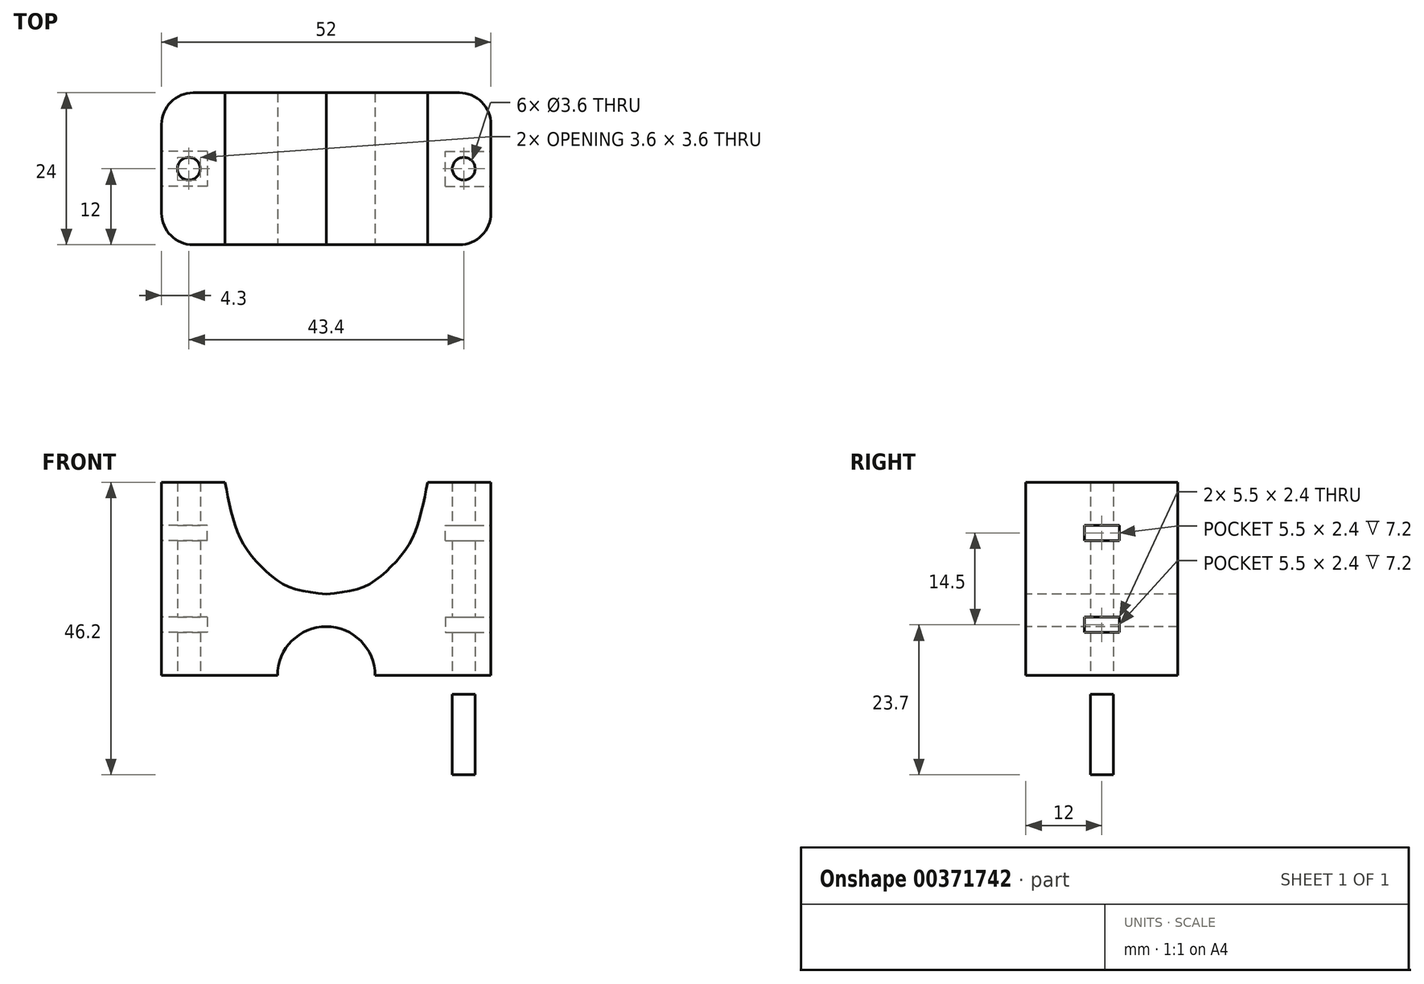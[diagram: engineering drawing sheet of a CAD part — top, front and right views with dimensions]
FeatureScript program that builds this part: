
annotation { "Feature Type Name" : "Feature", "Feature Type Description" : "" }
export const myFeature = defineFeature(function(context is Context, id is Id, definition is map)
    precondition{}
    {
        {
            var Q0;
            Q0=qCreatedBy(makeId("Top.planeOp"),FACE);
            var sketch = newSketch(context, id + "F0", { "sketchPlane" : qUnion([Q0])});
            skLineSegment(sketch, "E0.bottom", {"start": v(-21, 12) * mm, "end": v(21, 12) * mm});
            skLineSegment(sketch, "E0.top", {"start": v(-21, -12) * mm, "end": v(21, -12) * mm});
            skLineSegment(sketch, "E0.left", {"start": v(-26, 7) * mm, "end": v(-26, -7) * mm});
            skLineSegment(sketch, "E0.right", {"start": v(26, 7) * mm, "end": v(26, -7) * mm});
            skPoint(sketch, "E0.middle", {"position": v(0, 0) * mm});
            skLineSegment(sketch, "E1", {"start": v(0, 0) * mm, "end": v(-21.7, 0) * mm, "construction": true});
            skCircle(sketch, "E2", {"center": v(-21.7, 0) * mm, "radius": 1.8 * mm});
            skCircle(sketch, "E3.MirrorC", {"center": v(21.7, 0) * mm, "radius": 1.8 * mm});
            skPoint(sketch, "E4.visualSharp", {"position": v(-26, 12) * mm});
            skArc(sketch, "E4.filletArc", {"start": v(-21, 12) * mm, "mid": v(-24.54, 10.54) * mm, "end": v(-26, 7) * mm});
            skPoint(sketch, "E5.visualSharp", {"position": v(-26, -12) * mm});
            skArc(sketch, "E5.filletArc", {"start": v(-26, -7) * mm, "mid": v(-24.54, -10.54) * mm, "end": v(-21, -12) * mm});
            skPoint(sketch, "E6.visualSharp", {"position": v(26, -12) * mm});
            skArc(sketch, "E6.filletArc", {"start": v(21, -12) * mm, "mid": v(24.54, -10.54) * mm, "end": v(26, -7) * mm});
            skPoint(sketch, "E7.visualSharp", {"position": v(26, 12) * mm});
            skArc(sketch, "E7.filletArc", {"start": v(26, 7) * mm, "mid": v(24.54, 10.54) * mm, "end": v(21, 12) * mm});
            skSolve(sketch);
        }
        {
            var Q0;
            Q0 = qSketchRegion(id + "F0", true);
            extrude(context, id + "F1", {"entities" : qUnion([Q0]), "depth" : (15.7 / 2 + 22.65) * mm, "offsetDistance" : 25 * mm});
        }
        {
            var Q0;
            Q0=makeQuery(id+"F1.opExtrude","SWEPT_FACE",FACE,{"disambiguationData":[OSD([sQuery(id+"F0.wireOp",EDGE,"E0.top")])]});
            var sketch = newSketch(context, id + "F2", { "sketchPlane" : qUnion([Q0])});
            skArc(sketch, "E8", {"start": v(7.7, 0) * mm, "mid": v(0, 7.7) * mm, "end": v(-7.7, 0) * mm});
            skLineSegment(sketch, "E9", {"start": v(-7.7, 0) * mm, "end": v(-21, 0) * mm});
            skLineSegment(sketch, "E10", {"start": v(-21, 0) * mm, "end": v(-21, 30.5) * mm});
            skLineSegment(sketch, "E11", {"start": v(-21, 30.5) * mm, "end": v(-21, 30.5) * mm});
            skLineSegment(sketch, "E12", {"start": v(-21, 30.5) * mm, "end": v(-21, 0) * mm});
            skLineSegment(sketch, "E13", {"start": v(7.7, 0) * mm, "end": v(-21, 0) * mm});
            skLineSegment(sketch, "E14", {"start": v(0, 30.5) * mm, "end": v(0, 12.85) * mm, "construction": true});
            skLineSegment(sketch, "E15", {"start": v(16, 30.5) * mm, "end": v(0, 30.5) * mm});
            skLineSegment(sketch, "E16.MirrorCS", {"start": v(-16, 30.5) * mm, "end": v(0, 30.5) * mm});
            skFitSpline(sketch, "E17", {"points": [v(-16, 30.5) * mm, v(-14.81, 25.12) * mm, v(-12.95, 20.5) * mm, v(-9.64, 16.6) * mm, v(-5.78, 13.92) * mm, v(0, 12.85) * mm], "startDerivative": vector(5.26, -26.66) * mm, "endDerivative": vector(29.07, -2.83) * mm});
            skPoint(sketch, "E18.MirrorCS.start.orphan", {"position": v(-16, 12.85) * mm});
            skFitSpline(sketch, "E19.MirrorCS", {"points": [v(16, 30.5) * mm, v(14.81, 25.12) * mm, v(12.95, 20.5) * mm, v(9.64, 16.6) * mm, v(5.78, 13.92) * mm, v(0, 12.85) * mm], "startDerivative": vector(-5.26, -26.66) * mm, "endDerivative": vector(-29.07, -2.83) * mm});
            skPoint(sketch, "E20.start.orphan", {"position": v(16, 12.85) * mm});
            skSolve(sketch);
        }
        {
            var Q0;
            {var subQ0=sQuery(id+"F2.wireOp",EDGE,"E8");Q0=makeQuery(id+"F2.imprint","IMPRINT",FACE,{"disambiguationData":[TD([[makeQuery(id+"F2.imprint","IMPRINT",EDGE,{"derivedFrom":subQ0}),1.0]])]});}
            extrude(context, id + "F3", {"entities" : qUnion([Q0]), "operationType" : NewBodyOperationType.REMOVE, "oppositeDirection" : true, "depth" : 24 * mm, "offsetDistance" : 25 * mm});
        }
        {
            var Q0;
            Q0=makeQuery(id+"F2.imprint","IMPRINT",FACE,{"disambiguationData":[TD([[makeQuery(id+"F2.imprint","IMPRINT",EDGE,{"derivedFrom":sQuery(id+"F2.wireOp",EDGE,"E15")}),-1.0]])]});
            extrude(context, id + "F4", {"entities" : qUnion([Q0]), "operationType" : NewBodyOperationType.REMOVE, "oppositeDirection" : true, "depth" : 24 * mm, "offsetDistance" : 25 * mm});
        }
        {
            var Q0;
            Q0=makeQuery(id+"F1.opExtrude","SWEPT_FACE",FACE,{"disambiguationData":[OSD([sQuery(id+"F0.wireOp",EDGE,"E0.left")])]});
            var sketch = newSketch(context, id + "F5", { "sketchPlane" : qUnion([Q0])});
            skLineSegment(sketch, "E21", {"start": v(0, 0) * mm, "end": v(0, 8) * mm, "construction": true});
            skLineSegment(sketch, "E22.bottom", {"start": v(-2.75, 9.2) * mm, "end": v(2.75, 9.2) * mm});
            skLineSegment(sketch, "E22.top", {"start": v(-2.75, 6.8) * mm, "end": v(2.75, 6.8) * mm});
            skLineSegment(sketch, "E22.left", {"start": v(-2.75, 9.2) * mm, "end": v(-2.75, 6.8) * mm});
            skLineSegment(sketch, "E22.right", {"start": v(2.75, 9.2) * mm, "end": v(2.75, 6.8) * mm});
            skPoint(sketch, "E22.middle", {"position": v(0, 8) * mm});
            skLineSegment(sketch, "E23", {"start": v(-7, 15.25) * mm, "end": v(7, 15.25) * mm, "construction": true});
            skLineSegment(sketch, "E24.MirrorCS", {"start": v(-2.75, 21.3) * mm, "end": v(2.75, 21.3) * mm});
            skLineSegment(sketch, "E25.MirrorCS", {"start": v(2.75, 21.3) * mm, "end": v(2.75, 23.7) * mm});
            skLineSegment(sketch, "E26.MirrorCS", {"start": v(-2.75, 23.7) * mm, "end": v(2.75, 23.7) * mm});
            skLineSegment(sketch, "E27.MirrorCS", {"start": v(-2.75, 21.3) * mm, "end": v(-2.75, 23.7) * mm});
            skSolve(sketch);
        }
        {
            var Q0;
            Q0=makeQuery(id+"F5.imprint","IMPRINT",FACE,{"disambiguationData":[TD([[makeQuery(id+"F5.imprint","IMPRINT",EDGE,{"derivedFrom":sQuery(id+"F5.wireOp",EDGE,"E22.bottom")}),-1.0]])]});
            var Q1;
            Q1=makeQuery(id+"F5.imprint","IMPRINT",FACE,{"disambiguationData":[TD([[makeQuery(id+"F5.imprint","IMPRINT",EDGE,{"derivedFrom":sQuery(id+"F5.wireOp",EDGE,"E24.MirrorCS")}),1.0]])]});
            extrude(context, id + "F6", {"entities" : qUnion([Q0, Q1]), "operationType" : NewBodyOperationType.REMOVE, "oppositeDirection" : true, "depth" : (2.5 + 1.7 + 3) * mm, "offsetDistance" : 25 * mm});
        }
        {
            var Q0;
            Q0=makeQuery(id+"F1.opExtrude","SWEPT_FACE",FACE,{"disambiguationData":[OSD([sQuery(id+"F0.wireOp",EDGE,"E0.right")])]});
            var sketch = newSketch(context, id + "F7", { "sketchPlane" : qUnion([Q0])});
            skLineSegment(sketch, "E28", {"start": v(-7, 15.25) * mm, "end": v(7, 15.25) * mm, "construction": true});
            skLineSegment(sketch, "E29", {"start": v(0, 0) * mm, "end": v(0, 8) * mm, "construction": true});
            skLineSegment(sketch, "E30.bottom", {"start": v(-2.75, 9.2) * mm, "end": v(2.75, 9.2) * mm});
            skLineSegment(sketch, "E30.top", {"start": v(-2.75, 6.8) * mm, "end": v(2.75, 6.8) * mm});
            skLineSegment(sketch, "E30.left", {"start": v(-2.75, 9.2) * mm, "end": v(-2.75, 6.8) * mm});
            skLineSegment(sketch, "E30.right", {"start": v(2.75, 9.2) * mm, "end": v(2.75, 6.8) * mm});
            skPoint(sketch, "E30.middle", {"position": v(0, 8) * mm});
            skLineSegment(sketch, "E31.MirrorCS", {"start": v(-2.75, 21.3) * mm, "end": v(2.75, 21.3) * mm});
            skLineSegment(sketch, "E32.MirrorCS", {"start": v(2.75, 21.3) * mm, "end": v(2.75, 23.7) * mm});
            skLineSegment(sketch, "E33.MirrorCS", {"start": v(-2.75, 23.7) * mm, "end": v(2.75, 23.7) * mm});
            skLineSegment(sketch, "E34.MirrorCS", {"start": v(-2.75, 21.3) * mm, "end": v(-2.75, 23.7) * mm});
            skSolve(sketch);
        }
        {
            var Q0;
            Q0=makeQuery(id+"F7.imprint","IMPRINT",FACE,{"disambiguationData":[TD([[makeQuery(id+"F7.imprint","IMPRINT",EDGE,{"derivedFrom":sQuery(id+"F7.wireOp",EDGE,"E30.bottom")}),-1.0]])]});
            var Q1;
            Q1=makeQuery(id+"F7.imprint","IMPRINT",FACE,{"disambiguationData":[TD([[makeQuery(id+"F7.imprint","IMPRINT",EDGE,{"derivedFrom":sQuery(id+"F7.wireOp",EDGE,"E31.MirrorCS")}),1.0]])]});
            extrude(context, id + "F8", {"entities" : qUnion([Q0, Q1]), "operationType" : NewBodyOperationType.REMOVE, "oppositeDirection" : true, "depth" : (2.5 + 1.7 + 3) * mm, "offsetDistance" : 25 * mm});
        }
        {
            var Q0;
            Q0=qCreatedBy(makeId("Front.planeOp"),FACE);
            var sketch = newSketch(context, id + "F9", { "sketchPlane" : qUnion([Q0])});
            skLineSegment(sketch, "E35", {"start": v(0, 0) * mm, "end": v(0, -7.85) * mm, "construction": true});
            skLineSegment(sketch, "E36.bottom", {"start": v(-7.7, 0) * mm, "end": v(7.7, 0) * mm});
            skLineSegment(sketch, "E36.top", {"start": v(-26, -15.7) * mm, "end": v(26, -15.7) * mm});
            skLineSegment(sketch, "E36.left", {"start": v(-26, 0) * mm, "end": v(-26, -15.7) * mm});
            skLineSegment(sketch, "E36.right", {"start": v(26, -3) * mm, "end": v(26, -15.7) * mm});
            skPoint(sketch, "E36.middle", {"position": v(0, -7.85) * mm});
            skArc(sketch, "E37", {"start": v(-7.1, -3) * mm, "mid": v(0, -7.7) * mm, "end": v(7.1, -3) * mm});
            skLineSegment(sketch, "E38", {"start": v(-26, -3) * mm, "end": v(-7.1, -3) * mm});
            skLineSegment(sketch, "E39.MirrorCS", {"start": v(26, -3) * mm, "end": v(7.1, -3) * mm});
            skArc(sketch, "E40.trimOffspring", {"start": v(7.7, 0) * mm, "mid": v(0, 7.7) * mm, "end": v(-7.7, 0) * mm});
            skPoint(sketch, "E41.orphan", {"position": v(26, 0) * mm});
            skSolve(sketch);
        }
        {
            var Q0;
            Q0=makeQuery(id+"F9.imprint","IMPRINT",FACE,{"disambiguationData":[TD([[makeQuery(id+"F9.imprint","IMPRINT",EDGE,{"derivedFrom":sQuery(id+"F9.wireOp",EDGE,"E36.top")}),1.0]])]});
            extrude(context, id + "F10", {"entities" : qUnion([Q0]), "endBound" : BoundingType.SYMMETRIC, "depth" : 24 * mm, "offsetDistance" : 25 * mm});
        }
        {
            var Q0;
            Q0=makeQuery(id+"F10.opExtrude","SWEPT_FACE",FACE,{"disambiguationData":[OSD([sQuery(id+"F9.wireOp",EDGE,"E36.top")])]});
            var sketch = newSketch(context, id + "F11", { "sketchPlane" : qUnion([Q0])});
            skLineSegment(sketch, "E42.bottom", {"start": v(-21, 12) * mm, "end": v(21, 12) * mm});
            skLineSegment(sketch, "E42.top", {"start": v(-21, -12) * mm, "end": v(21, -12) * mm});
            skLineSegment(sketch, "E42.left", {"start": v(-26, 7) * mm, "end": v(-26, -7) * mm});
            skLineSegment(sketch, "E42.right", {"start": v(26, 7) * mm, "end": v(26, -7) * mm});
            skPoint(sketch, "E43.visualSharp", {"position": v(-26, 12) * mm});
            skArc(sketch, "E43.filletArc", {"start": v(-21, 12) * mm, "mid": v(-24.54, 10.54) * mm, "end": v(-26, 7) * mm});
            skPoint(sketch, "E44.visualSharp", {"position": v(-26, -12) * mm});
            skArc(sketch, "E44.filletArc", {"start": v(-26, -7) * mm, "mid": v(-24.54, -10.54) * mm, "end": v(-21, -12) * mm});
            skPoint(sketch, "E45.visualSharp", {"position": v(26, -12) * mm});
            skArc(sketch, "E45.filletArc", {"start": v(21, -12) * mm, "mid": v(24.54, -10.54) * mm, "end": v(26, -7) * mm});
            skPoint(sketch, "E46.visualSharp", {"position": v(26, 12) * mm});
            skArc(sketch, "E46.filletArc", {"start": v(26, 7) * mm, "mid": v(24.54, 10.54) * mm, "end": v(21, 12) * mm});
            skSolve(sketch);
        }
        {
            var Q0;
            {var subQ0=sQuery(id+"F11.wireOp",EDGE,"E46.filletArc");Q0=makeQuery(id+"F11.imprint","IMPRINT",FACE,{"disambiguationData":[TD([[makeQuery(id+"F11.imprint","IMPRINT",EDGE,{"derivedFrom":subQ0}),-1.0]])]});}
            var Q1;
            {var subQ0=sQuery(id+"F11.wireOp",EDGE,"E45.filletArc");Q1=makeQuery(id+"F11.imprint","IMPRINT",FACE,{"disambiguationData":[TD([[makeQuery(id+"F11.imprint","IMPRINT",EDGE,{"derivedFrom":subQ0}),-1.0]])]});}
            var Q2;
            {var subQ0=sQuery(id+"F11.wireOp",EDGE,"E44.filletArc");Q2=makeQuery(id+"F11.imprint","IMPRINT",FACE,{"disambiguationData":[TD([[makeQuery(id+"F11.imprint","IMPRINT",EDGE,{"derivedFrom":subQ0}),-1.0]])]});}
            var Q3;
            {var subQ0=sQuery(id+"F11.wireOp",EDGE,"E43.filletArc");Q3=makeQuery(id+"F11.imprint","IMPRINT",FACE,{"disambiguationData":[TD([[makeQuery(id+"F11.imprint","IMPRINT",EDGE,{"derivedFrom":subQ0}),-1.0]])]});}
            extrude(context, id + "F12", {"entities" : qUnion([Q0, Q1, Q2, Q3]), "operationType" : NewBodyOperationType.REMOVE, "oppositeDirection" : true, "depth" : 15.7 * mm, "offsetDistance" : 25 * mm});
        }
        {
            var Q0;
            Q0=makeQuery(id+"F0.imprint","IMPRINT",FACE,{"disambiguationData":[TD([[makeQuery(id+"F0.imprint","IMPRINT",EDGE,{"derivedFrom":sQuery(id+"F0.wireOp",EDGE,"E2")}),1.0]])]});
            var Q1;
            Q1=makeQuery(id+"F0.imprint","IMPRINT",FACE,{"disambiguationData":[TD([[makeQuery(id+"F0.imprint","IMPRINT",EDGE,{"derivedFrom":sQuery(id+"F0.wireOp",EDGE,"E3.MirrorC")}),-1.0]])]});
            extrude(context, id + "F13", {"entities" : qUnion([Q0, Q1]), "operationType" : NewBodyOperationType.REMOVE, "oppositeDirection" : true, "depth" : 25 * mm, "offsetDistance" : 25 * mm});
        }
    });
